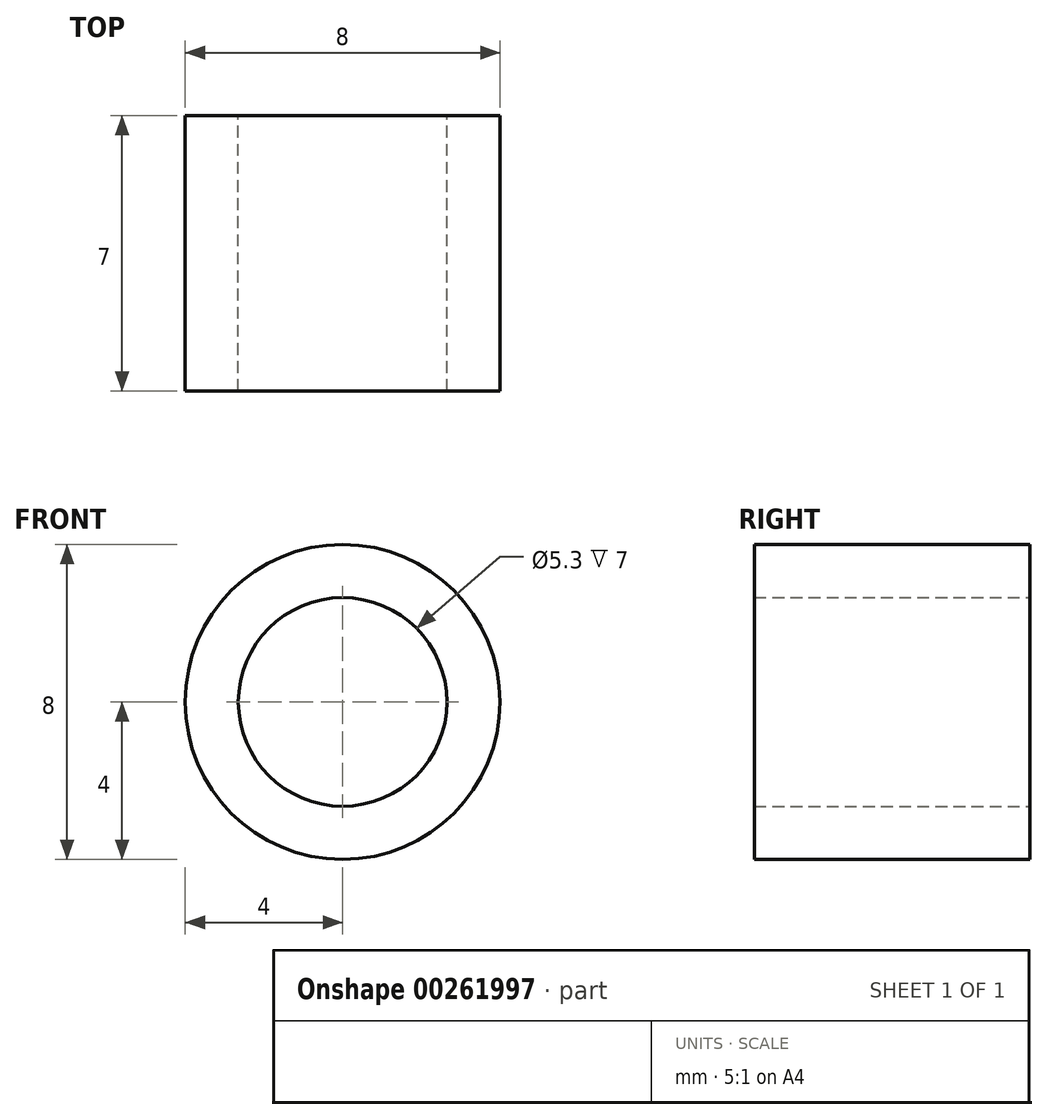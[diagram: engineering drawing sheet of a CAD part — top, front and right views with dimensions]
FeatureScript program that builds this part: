
annotation { "Feature Type Name" : "Feature", "Feature Type Description" : "" }
export const myFeature = defineFeature(function(context is Context, id is Id, definition is map)
    precondition{}
    {
        {
            assignVariable(context, id + "F0", {"name" : "Hieght", "anyValue" : 7});
        }
        {
            var Q0;
            Q0=qCreatedBy(makeId("Front.planeOp"),FACE);
            var sketch = newSketch(context, id + "F1", { "sketchPlane" : qUnion([Q0])});
            skCircle(sketch, "E0", {"center": v(0, 0) * mm, "radius": 2.65 * mm});
            skCircle(sketch, "E1", {"center": v(0, 0) * mm, "radius": 4 * mm});
            skSolve(sketch);
        }
        {
            var Q0;
            Q0=makeQuery(id+"F1.imprint","IMPRINT",FACE,{"disambiguationData":[TD([[makeQuery(id+"F1.imprint","IMPRINT",EDGE,{"derivedFrom":sQuery(id+"F1.wireOp",EDGE,"E0")}),-1.0]])]});
            extrude(context, id + "F2", {"entities" : qUnion([Q0]), "depth" : getVariable(context, 'Hieght') * mm});
        }
    });
